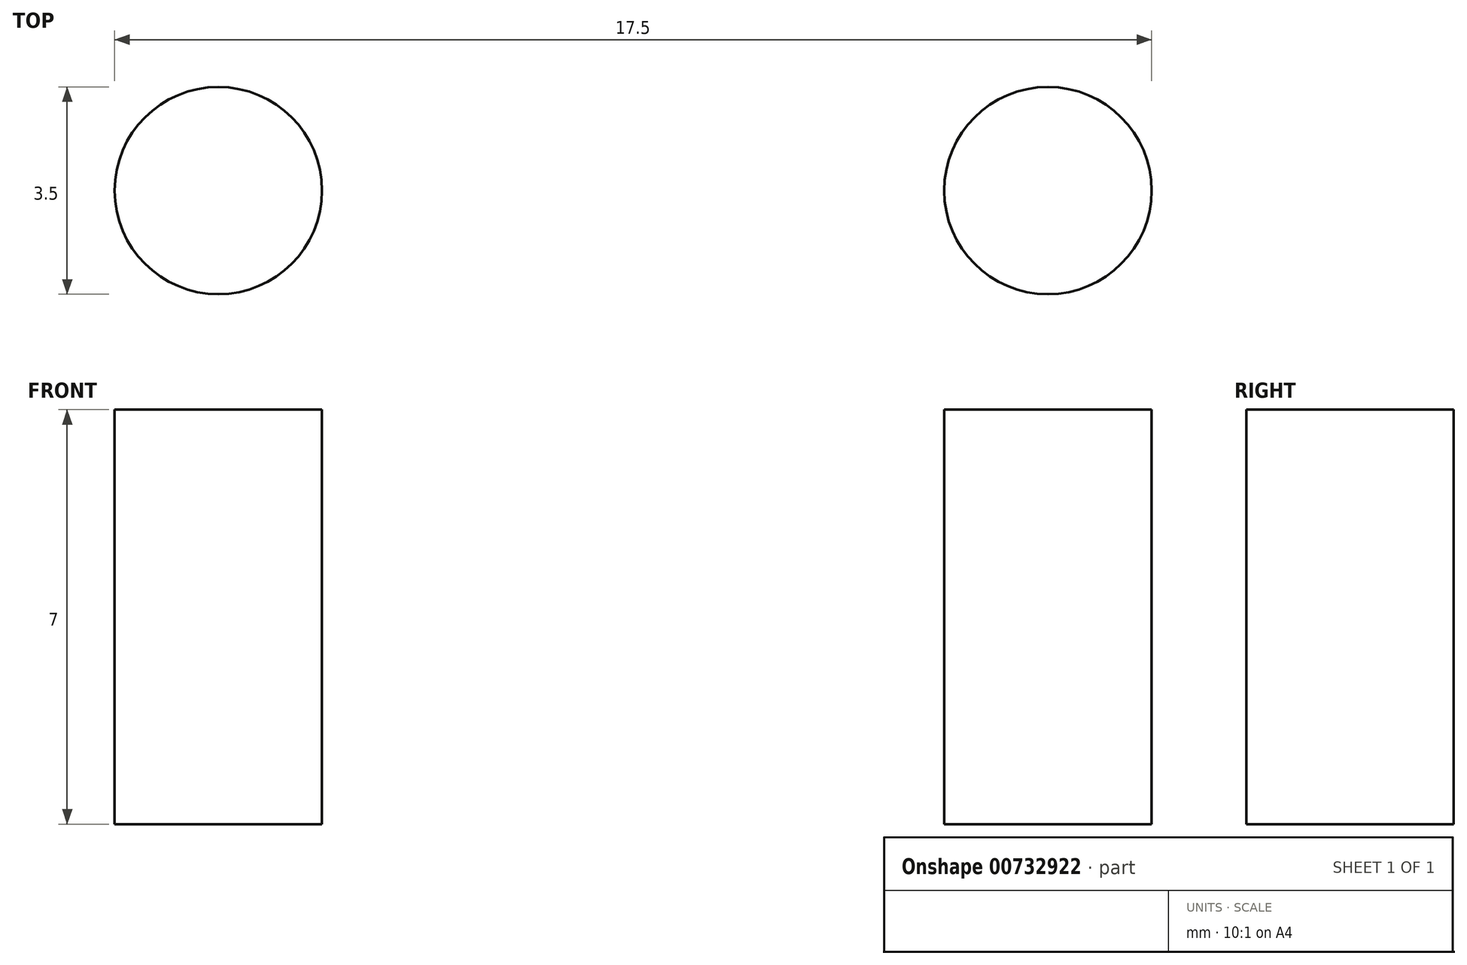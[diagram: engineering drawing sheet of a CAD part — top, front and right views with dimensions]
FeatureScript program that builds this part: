
annotation { "Feature Type Name" : "Feature", "Feature Type Description" : "" }
export const myFeature = defineFeature(function(context is Context, id is Id, definition is map)
    precondition{}
    {
        {
            var Q0;
            Q0=qCreatedBy(makeId("Top.planeOp"),FACE);
            var sketch = newSketch(context, id + "F0", { "sketchPlane" : qUnion([Q0])});
            skCircle(sketch, "E0", {"center": v(0, 0) * mm, "radius": 30 * mm});
            skSolve(sketch);
        }
        {
            var Q0;
            Q0 = qSketchRegion(id + "F0", true);
            extrude(context, id + "F1", {"entities" : qUnion([Q0]), "depth" : 15 * mm, "offsetDistance" : 25 * mm});
        }
        {
            var Q0;
            Q0=makeQuery(id+"F1.opExtrude","CAP_FACE",FACE,{"disambiguationData":[OSD([sQuery(id+"F0.wireOp",EDGE,"E0")])],"isStart":false});
            var sketch = newSketch(context, id + "F2", { "sketchPlane" : qUnion([Q0])});
            skLineSegment(sketch, "E1.bottom", {"start": v(-7, 6.66) * mm, "end": v(7, 6.66) * mm});
            skLineSegment(sketch, "E1.top", {"start": v(-7, -6.66) * mm, "end": v(7, -6.66) * mm});
            skLineSegment(sketch, "E1.left", {"start": v(-7, 6.66) * mm, "end": v(-7, -6.66) * mm});
            skLineSegment(sketch, "E1.right", {"start": v(7, 6.66) * mm, "end": v(7, -6.66) * mm});
            skPoint(sketch, "E1.middle", {"position": v(0, 0) * mm});
            skCircle(sketch, "E2", {"center": v(-7, 0) * mm, "radius": 1.75 * mm});
            skCircle(sketch, "E3", {"center": v(7, 0) * mm, "radius": 1.75 * mm});
            skSolve(sketch);
        }
        {
            var Q0;
            {var subQ0=sQuery(id+"F2.wireOp",EDGE,"E2");var subQ1=sQuery(id+"F2.wireOp",EDGE,"E1.left");var subQ2=makeQuery(id+"F2.imprint","INTERSECT",VERTEX,{"disambiguationData":[OD(0.0)],"derivedFrom":[subQ1,subQ0]});Q0=makeQuery(id+"F2.imprint","IMPRINT",FACE,{"disambiguationData":[TD([[makeQuery(id+"F2.imprint","IMPRINT",EDGE,{"disambiguationData":[TD([[subQ2,-1.0]])],"derivedFrom":subQ1}),1.0]])]});}
            var Q1;
            {var subQ0=sQuery(id+"F2.wireOp",EDGE,"E2");var subQ1=sQuery(id+"F2.wireOp",EDGE,"E1.left");var subQ2=makeQuery(id+"F2.imprint","INTERSECT",VERTEX,{"disambiguationData":[OD(0.0)],"derivedFrom":[subQ1,subQ0]});Q1=makeQuery(id+"F2.imprint","IMPRINT",FACE,{"disambiguationData":[TD([[makeQuery(id+"F2.imprint","IMPRINT",EDGE,{"disambiguationData":[TD([[subQ2,-1.0]])],"derivedFrom":subQ1}),-1.0]])]});}
            var Q2;
            {var subQ0=sQuery(id+"F2.wireOp",EDGE,"E3");var subQ1=sQuery(id+"F2.wireOp",EDGE,"E1.right");var subQ2=makeQuery(id+"F2.imprint","INTERSECT",VERTEX,{"disambiguationData":[OD(0.0)],"derivedFrom":[subQ1,subQ0]});Q2=makeQuery(id+"F2.imprint","IMPRINT",FACE,{"disambiguationData":[TD([[makeQuery(id+"F2.imprint","IMPRINT",EDGE,{"disambiguationData":[TD([[subQ2,-1.0]])],"derivedFrom":subQ1}),-1.0]])]});}
            var Q3;
            {var subQ0=sQuery(id+"F2.wireOp",EDGE,"E3");var subQ1=sQuery(id+"F2.wireOp",EDGE,"E1.right");var subQ2=makeQuery(id+"F2.imprint","INTERSECT",VERTEX,{"disambiguationData":[OD(0.0)],"derivedFrom":[subQ1,subQ0]});Q3=makeQuery(id+"F2.imprint","IMPRINT",FACE,{"disambiguationData":[TD([[makeQuery(id+"F2.imprint","IMPRINT",EDGE,{"disambiguationData":[TD([[subQ2,-1.0]])],"derivedFrom":subQ1}),1.0]])]});}
            extrude(context, id + "F3", {"entities" : qUnion([Q0, Q1, Q2, Q3]), "operationType" : NewBodyOperationType.REMOVE, "oppositeDirection" : true, "depth" : 25 * mm, "offsetDistance" : 25 * mm});
        }
        {
            var Q0;
            Q0=makeQuery(id+"F1.opExtrude","CAP_FACE",FACE,{"disambiguationData":[OSD([sQuery(id+"F0.wireOp",EDGE,"E0")])],"isStart":false});
            var sketch = newSketch(context, id + "F4", { "sketchPlane" : qUnion([Q0])});
            skCircle(sketch, "E4", {"center": v(0, 0) * mm, "radius": 23 * mm});
            skSolve(sketch);
        }
        {
            var Q0;
            Q0 = qSketchRegion(id + "F4", true);
            extrude(context, id + "F5", {"entities" : qUnion([Q0]), "operationType" : NewBodyOperationType.REMOVE, "oppositeDirection" : true, "depth" : 5 * mm, "offsetDistance" : 25 * mm});
        }
        {
            var Q0;
            Q0=makeQuery(id+"F5.boolean.opBoolean","COPY",FACE,{"derivedFrom":makeQuery(id+"F5.opExtrude","CAP_FACE",FACE,{"disambiguationData":[OSD([sQuery(id+"F4.wireOp",EDGE,"E4")])],"isStart":false})});
            var sketch = newSketch(context, id + "F6", { "sketchPlane" : qUnion([Q0])});
            skCircle(sketch, "E5", {"center": v(0, 0) * mm, "radius": 12 * mm});
            skSolve(sketch);
        }
        {
            var Q0;
            Q0 = qSketchRegion(id + "F6", true);
            extrude(context, id + "F7", {"entities" : qUnion([Q0]), "operationType" : NewBodyOperationType.REMOVE, "oppositeDirection" : true, "depth" : 3 * mm, "offsetDistance" : 25 * mm});
        }
        {
            var Q0;
            Q0=makeQuery(id+"F1.opExtrude","CAP_FACE",FACE,{"disambiguationData":[OSD([sQuery(id+"F0.wireOp",EDGE,"E0")])],"isStart":true});
            var sketch = newSketch(context, id + "F8", { "sketchPlane" : qUnion([Q0])});
            skCircle(sketch, "E6", {"center": v(0, 0) * mm, "radius": 3.5 * mm});
            skSolve(sketch);
        }
        {
            var Q0;
            Q0=makeQuery(id+"F8.imprint","IMPRINT",FACE,{"disambiguationData":[TD([[makeQuery(id+"F8.imprint","IMPRINT",EDGE,{"derivedFrom":sQuery(id+"F8.wireOp",EDGE,"E6")}),1.0]])]});
            extrude(context, id + "F9", {"entities" : qUnion([Q0]), "operationType" : NewBodyOperationType.REMOVE, "oppositeDirection" : true, "depth" : 25 * mm, "offsetDistance" : 25 * mm});
        }
    });
